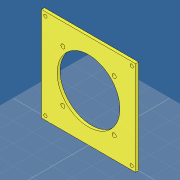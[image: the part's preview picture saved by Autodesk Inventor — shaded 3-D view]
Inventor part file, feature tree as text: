
AUTODESK INVENTOR PART (.ipt)
format: ipt  version: 2019 (Build 230136000, 136)  size: 109,568 bytes
history: native  units: mm
features: hole x2, sketch x1, extrude x1
ambient origin geometry x8: Origin, YZ Plane, XZ Plane, XY Plane, X Axis, Y Axis, Z Axis, Center Point
bodies: Volumenkörper1 (feature_tree)
feature tree (4):
  sketch  "Skizze1"  dims[d0=96.0mm d1=96.0mm d27=3.0mm d28=0.0mm d41=64.0mm d42=74.0mm d43=8.0mm d44=8.0mm d45=3.4mm d46=6.0mm d47=4.0mm d48=2.0mm d49=90.0deg d50=8.0mm d51=20.594885mm d52=4.2mm d53=6.0mm d54=4.0mm d55=2.0mm d56=90.0deg d57=8.0mm d58=20.594885mm]
  extrude  "Extrusion1"  Depth=96.0mm
  hole  "Bohrung2"  [1 undecoded]
  hole  "Bohrung3"  [1 undecoded]
note: 2 required parameter values undecoded (feature->parameter linkage not recoverable at this tier; creation-order binding heuristic only, values carry confidence <= 0.55)
